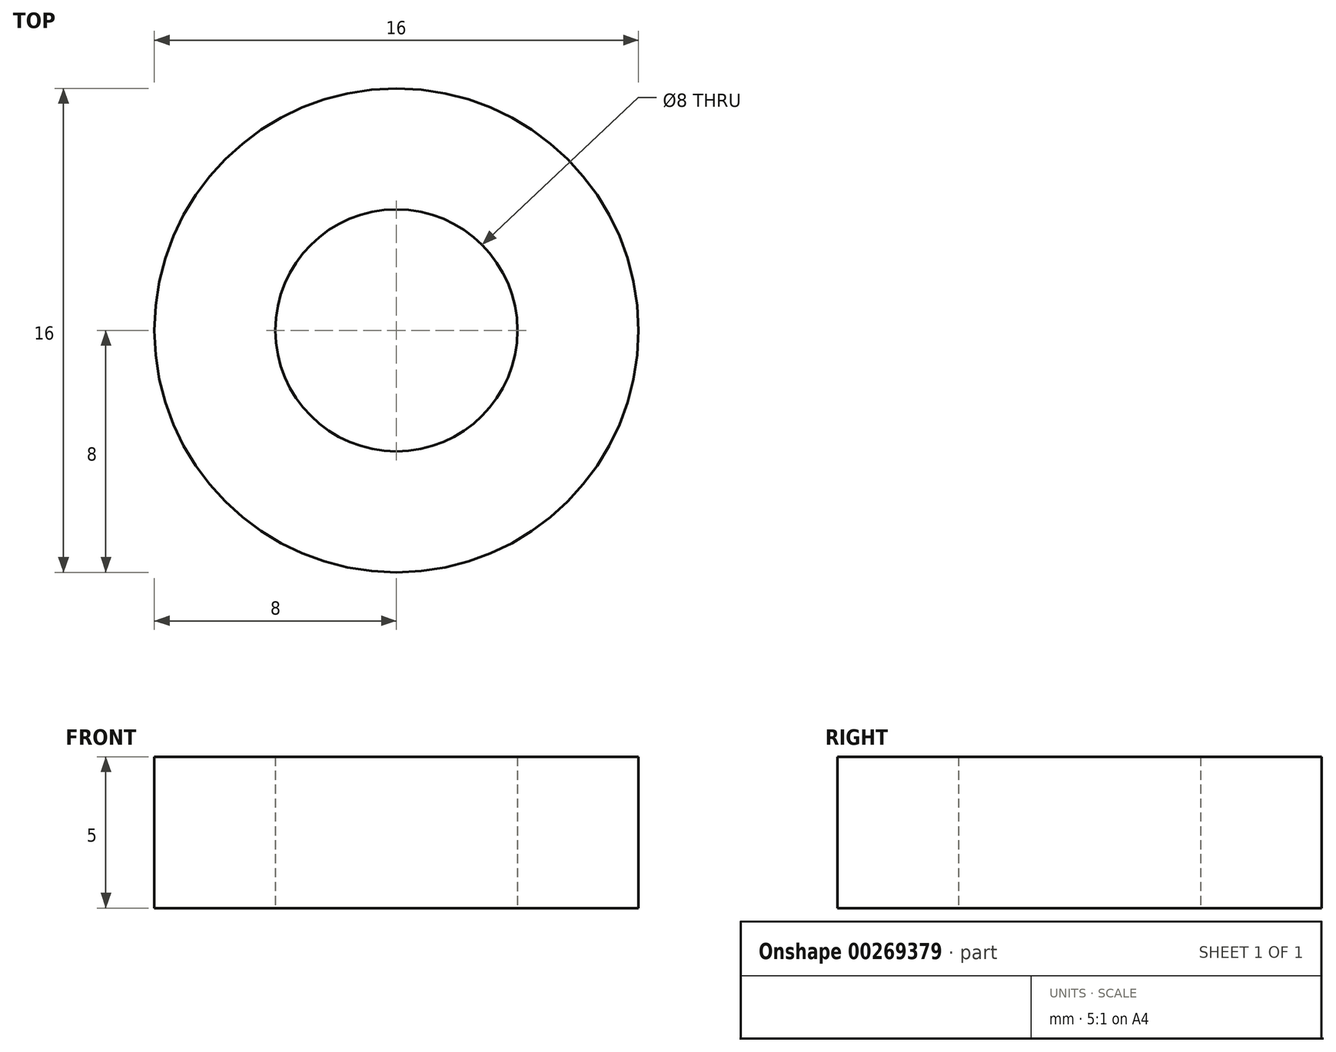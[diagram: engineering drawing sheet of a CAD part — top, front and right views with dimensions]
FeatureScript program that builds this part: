
annotation { "Feature Type Name" : "Feature", "Feature Type Description" : "" }
export const myFeature = defineFeature(function(context is Context, id is Id, definition is map)
    precondition{}
    {
        {
            var Q0;
            Q0=qCreatedBy(makeId("Top.planeOp"),FACE);
            var sketch = newSketch(context, id + "F0", { "sketchPlane" : qUnion([Q0])});
            skCircle(sketch, "E0", {"center": v(0, 0) * mm, "radius": 8 * mm});
            skCircle(sketch, "E1", {"center": v(0, 0) * mm, "radius": 4 * mm});
            skSolve(sketch);
        }
        {
            var Q0;
            Q0=makeQuery(id+"F0.imprint","IMPRINT",FACE,{"disambiguationData":[TD([[makeQuery(id+"F0.imprint","IMPRINT",EDGE,{"derivedFrom":sQuery(id+"F0.wireOp",EDGE,"E0")}),1.0]])]});
            extrude(context, id + "F1", {"entities" : qUnion([Q0]), "endBound" : BoundingType.SYMMETRIC, "depth" : 5 * mm});
        }
    });
